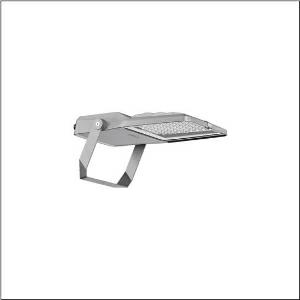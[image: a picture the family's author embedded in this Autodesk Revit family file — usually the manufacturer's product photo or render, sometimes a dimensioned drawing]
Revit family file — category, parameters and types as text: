
# Revit family: floodlight_fl_21_iq_mini___pl52_5xa7771d2d1a_936e
name_source: partatom
category: Lighting Fixtures
units: mm (PartAtom-declared; Revit-internal decimal feet)

## family parameters
Cut with Voids When Loaded = No
Host = Face
Light Source = No
Part Type = Normal
Room Calculation Point = No
Round Connector Dimension = Use Diameter
Shared = No

## types (1)
- --- (1 x LED, 17830 lm, 143 W, 3000K)
    Apparent Load = 143 VA
    CIE Flux Codes = 26 60 98 100 100
    Color Rendering = 70
    Color Temperature = 3000K
    Default Elevation = 1800 mm
    Description = Floodlight FL 21 iQ mini, floodlight, primary light control with lens, of PMMA, primary optical cover: protective disc, of toughened safety glass, transparent, light distribution: PL52, light emission: direct distribution, installation type: surface-mounted, lamps: LED, High Power LED, rated values: 17.830lm | 143W | 124,7lm/W (begin service life); end service life: 17.830lm | 151,6W; at 50% lumin. flux: 8.915lm | 60,6W | 147,1lm/W, colour temperature: 3000K, colour rendering: CRI > 70, light colour: 730, light setting 1 begin service life: 100% | 17.830lm | 143W | 124,7lm/W | 3.000K, light setting 1 end service life: 151,6W, further light settings possible, control: Auto-Match, Temp-Guard, Lumen-Switch, Night-Set, Smart-Wire, Light-Fading, Desk-Remote (wireless, voltage-free reading and setting of iQ features in the workshop via application-optimized NFC function/RFID function), optimised constant luminous flux control (CLO 2.0), pre-setting: linear dimming characteristic, with terminal, 6-pole, mains connection: 220..240V, AC, 50/60Hz, luminaire housing, of diecast aluminium, powder-coated, SITECO metallic grey (DB 702S), corrosivity category C5 mid according to DIN EN ISO 12944suitable for swimming poolschlorine-resistant, sealing non-destructively replaceable, mounting bracket, of steel, galvanised, powder-coated, SITECO metallic grey (DB 702S), protection rating (complete): IP66, insulation class (complete): insulation class II (safety insulation), certification: CE, ENEC, VDE, protection symbol: D, impact resistance: IK08, permissible operating ambient temperature: -40..+40°C, permissible operating ambient temperature for outdoor applications: -40..+50°C, standard: DIN EN 12944, LABS conformity tested according to VDMA 24364:2018-05, packaging unit: 1 piece

Light Distribution: PL52
    Height = 70 mm
    Lamp = 1 x LED
    Lamp Light Flux = 17830 lm
    Lamp Power = 143 W
    Lamp count = 1
    Length = 485 mm
    Luminous efficacy = 125 lm/W
    Manufacturer = Siteco
    ModVariant = No
    Model = 5XA7771D2D1A
    Number of Poles = 1
    OnlyDefault = Yes
    Power Factor = 1
    Product Name = Floodlight FL 21 iQ mini | PL52
    Product group = floodlight | pylon annexe
    ProductGroupID = 6201
    Protection Class = Protection class II
    Protection Degree = IP 66
    RLX_Detail_Level = 1
    RLX_Emergency_Light_Flux = 0 lm
    RLX_Emergency_Type = 0
    RLX_Emergency_Type_DB = No
    RlxData = <blob elided: 96981 chars, md5=517f6f71>
    Socket = socket
    Standby Power = 0 W
    System Light Flux = 17830 lm
    System Power = 143 W
    Type Comments = factory setting: luminous flux: 100 % | dim-lin: 254 | 730 mA
    Type Image = l_1006845.jpg
    URL = http://relux.com
    VarID = @adj_163523
    Voltage = 0 V
    Weight = 0.00 kg
    Width = 337 mm

## geometry (parser evidence)
native form markers: Blend x4, Sweep x11
no freeform markers — native parametric forms only
